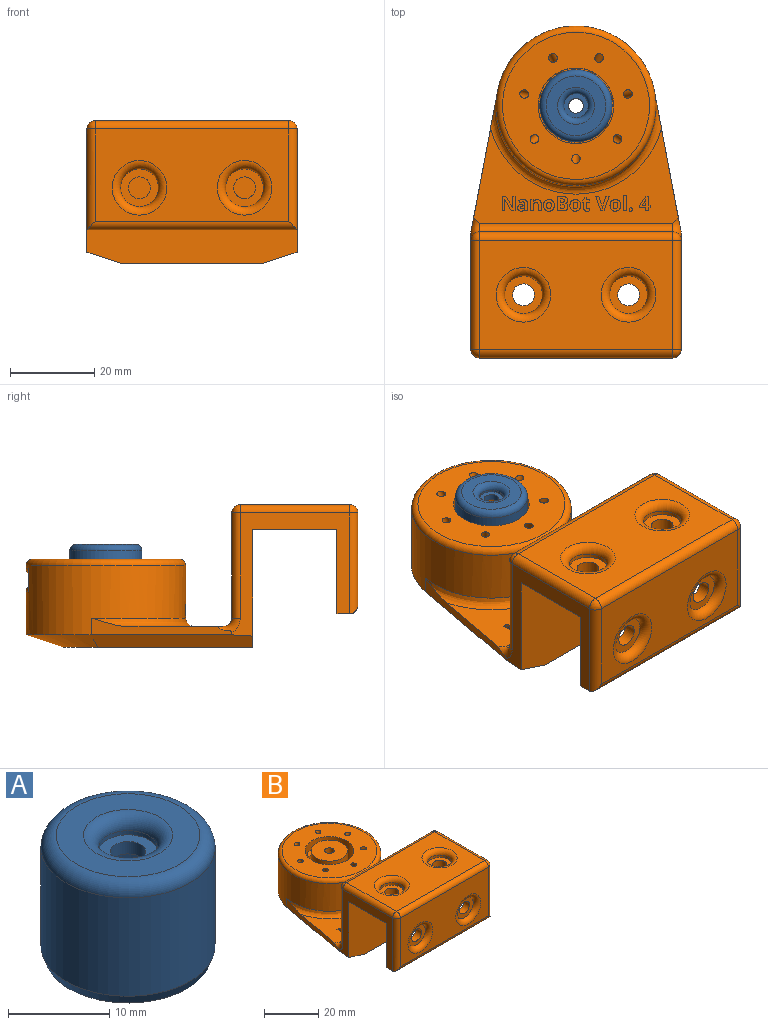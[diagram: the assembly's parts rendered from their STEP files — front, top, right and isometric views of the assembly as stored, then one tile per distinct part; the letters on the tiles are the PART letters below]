
ASSEMBLY  parts=2 mates=1
PART A: 12 faces, bbox 18.6x18.6x14.5 mm
  f0: cylinder r=1.75mm len=3.5mm, axis (0,0,-1), area 16.5mm2, adj f1,f7
  f1: plane 14.3x14.3mm, normal (0,0,-1), area 151mm2, adj f0,f4
  f2: cylinder r=8.6mm len=17.2mm, axis (0,0,-1), area 643.1mm2, adj f9,f11
  f3: plane 14.2x14.2mm, normal (0,0,1), area 97.5mm2, adj f10,f11
  f4: cylinder r=7.15mm len=14.3mm, axis (0,0,1), area 444.8mm2, adj f1,f8
  f5: plane 16.4x16.4mm, normal (0,0,-1), area 32.2mm2, adj f8,f9
  f6: cylinder r=2.9mm len=5.8mm, axis (0,0,1), area 9.1mm2, adj f7,f10
  f7: plane 5.8x5.8mm, normal (0,0,1), area 16.8mm2, adj f0,f6
  f8: cone r=7.55mm half-angle=20deg, axis (0,0,-1), area 54mm2, adj f4,f5
  f9: cone r=8.6mm half-angle=20deg, axis (0,0,1), area 61.7mm2, adj f2,f5
  f10: torus R=4.4mm, axis (0,0,1), area 51mm2, adj f3,f6
  f11: torus R=7.1mm, axis (0,0,1), area 119.2mm2, adj f2,f3
PART B: 294 faces, bbox 50.4x81x35.1 mm
  f0: plane 5.6x5.13mm, normal (0,0,1), area 23.1mm2, adj f2,f3,f282,f283,f288
  f1: plane 13.5x13.5mm, normal (0,0,1), area 133.5mm2, adj f275,f288
  f2: plane 10.14x5mm, normal (1,0,0), area 33.4mm2, adj f0,f4,f278,f280,f281,f283,f284,f288
  f3: plane 10.14x5mm, normal (-1,0,0), area 33.4mm2, adj f0,f4,f278,f280,f281,f282,f285,f288
  f4: plane 10.75x5.6mm, normal (0,0,-1), area 49.5mm2, adj f2,f3,f275,f280,f288
  f5: plane 8.95x5.66mm, normal (0,0,1), area 48mm2, adj f276,f277,f287,f289,f291,f292
  f6: cylinder r=1.75mm len=12.25mm, axis (0,0,1), area 134.7mm2, adj f33,f281
  f7: cylinder r=1mm len=22.37mm, axis (-0.27,-0.21,0.94), area 130.9mm2, adj f33,f35,f286,f287
  f8: cylinder r=1mm len=22.37mm, axis (-0.33,0.08,0.94), area 130.9mm2, adj f33,f35,f286,f287
  f9: cylinder r=1mm len=22.37mm, axis (-0.15,0.31,0.94), area 130.9mm2, adj f33,f35,f286,f287
  f10: cylinder r=1mm len=22.37mm, axis (0.15,0.31,0.94), area 130.9mm2, adj f33,f35,f286,f287
  f11: cylinder r=1mm len=22.37mm, axis (0.33,0.08,0.94), area 130.9mm2, adj f33,f35,f286,f287
  f12: cylinder r=1mm len=22.37mm, axis (0.27,-0.21,0.94), area 130.9mm2, adj f33,f35,f286,f287
  f13: plane 48.78x22.84mm, normal (0,0,1), area 488.2mm2, adj f36,f37,f38,f39,f44,f57,f62,f63
  f14: plane 29.31x28mm, normal (1,0,0), area 242.9mm2, adj f17,f21,f29,f32,f37,f40,f43,f44
  f15: plane 29.31x28mm, normal (-1,0,0), area 242.9mm2, adj f17,f21,f29,f32,f36,f42,f50,f54
  f16: plane 46x25mm, normal (0,1,0), area 1150mm2, adj f39,f47,f53,f56
  f17: plane 50x20mm, normal (0,0,-1), area 957.5mm2, adj f14,f15,f21,f22,f23,f32
  f18: plane 46x22mm, normal (0,-1,0), area 746.5mm2, adj f43,f46,f49,f50,f58,f59
  f19: cylinder r=2.6mm len=5.2mm, axis (0,-1,0), area 49mm2, adj f21,f31
  f20: cylinder r=2.6mm len=5.2mm, axis (0,-1,0), area 49mm2, adj f21,f30
  f21: plane 50x20mm, normal (0,1,0), area 957.5mm2, adj f14,f15,f17,f19,f20,f29
  f22: cylinder r=2.6mm len=5.2mm, axis (0,0,1), area 49mm2, adj f17,f28
  f23: cylinder r=2.6mm len=5.2mm, axis (0,0,1), area 49mm2, adj f17,f26
  f24: plane 46x26mm, normal (0,0,1), area 930.5mm2, adj f48,f49,f53,f54,f60,f61
  f25: cylinder r=4.5mm len=9mm, axis (0,0,1), area 28.3mm2, adj f26,f60
  f26: plane 9x9mm, normal (0,0,1), area 42.4mm2, adj f23,f25
  f27: cylinder r=4.5mm len=9mm, axis (0,0,1), area 28.3mm2, adj f28,f61
  f28: plane 9x9mm, normal (0,0,1), area 42.4mm2, adj f22,f27
  f29: plane 50x3mm, normal (0,0,-1), area 150mm2, adj f14,f15,f21,f46
  f30: plane 9x9mm, normal (0,-1,0), area 42.4mm2, adj f20,f59
  f31: plane 9x9mm, normal (0,-1,0), area 42.4mm2, adj f19,f58
  f32: plane 50x28mm, normal (0,-1,0), area 1377.9mm2, adj f14,f15,f17,f33,f40,f42
  f33: plane 45x33.57mm, normal (0,0,-1), area 1067.9mm2, adj f6,f7,f8,f9,f10,f11,f12,f32
  f34: cylinder r=19mm len=38mm, axis (0,0,-1), area 1650.8mm2, adj f36,f37,f38,f41,f289,f290,f291,f292
  f35: plane 35x35mm, normal (0,0,1), area 684.2mm2, adj f7,f8,f9,f10,f11,f12,f274,f287
  f36: plane 33.93x6.74mm, normal (-0.98,0.19,0), area 72.3mm2, adj f13,f15,f34,f38,f42,f57
  f37: plane 33.93x6.74mm, normal (0.98,0.19,0), area 72.3mm2, adj f13,f14,f34,f38,f40,f44
  f38: torus R=21mm, axis (0,0,1), area 190.1mm2, adj f13,f34,f36,f37
  f39: cylinder r=2mm len=46mm, axis (1,0,0), area 144.5mm2, adj f13,f16,f44,f57
  f40: plane 38.53x15.17mm, normal (0.31,0.06,-0.95), area 361.4mm2, adj f14,f32,f33,f37,f41
  f41: cone r=10mm half-angle=71.6deg, axis (0,0,1), area 380.8mm2, adj f33,f34,f40,f42
  f42: plane 38.53x15.17mm, normal (-0.31,0.06,-0.95), area 361.4mm2, adj f15,f32,f33,f36,f41
  f43: cylinder r=2mm len=24mm, axis (0,0,-1), area 73.1mm2, adj f14,f18,f45,f46
  f44: torus R=4mm, axis (1,0,0), area 13.1mm2, adj f13,f14,f37,f39,f47
  f45: sphere r=2mm, area 6.3mm2, adj f43,f48,f49
  f46: cylinder r=2mm len=50mm, axis (1,0,0), area 152.5mm2, adj f18,f29,f43,f50
  f47: cylinder r=2mm len=25mm, axis (0,0,1), area 78.5mm2, adj f14,f16,f44,f51
  f48: cylinder r=2mm len=26mm, axis (0,1,0), area 81.7mm2, adj f14,f24,f45,f51
  f49: cylinder r=2mm len=46mm, axis (1,0,0), area 144.5mm2, adj f18,f24,f45,f52
  f50: cylinder r=2mm len=24mm, axis (0,0,1), area 73.1mm2, adj f15,f18,f46,f52
  f51: sphere r=2mm, area 6.3mm2, adj f47,f48,f53
  f52: sphere r=2mm, area 6.3mm2, adj f49,f50,f54
  f53: cylinder r=2mm len=46mm, axis (-1,0,0), area 144.5mm2, adj f16,f24,f51,f55
  f54: cylinder r=2mm len=26mm, axis (0,-1,0), area 81.7mm2, adj f15,f24,f52,f55
  f55: sphere r=2mm, area 6.3mm2, adj f53,f54,f56
  f56: cylinder r=2mm len=25mm, axis (0,0,-1), area 78.5mm2, adj f15,f16,f55,f57
  f57: torus R=4mm, axis (1,0,0), area 13.1mm2, adj f13,f15,f36,f39,f56
  f58: torus R=6.5mm, axis (0,1,0), area 103.2mm2, adj f18,f31
  f59: torus R=6.5mm, axis (0,1,0), area 103.2mm2, adj f18,f30
  f60: torus R=6.5mm, axis (0,0,1), area 103.2mm2, adj f24,f25
  f61: torus R=6.5mm, axis (0,0,1), area 103.2mm2, adj f24,f27
  f62: extruded ~1x0.3mm, area 0.3mm2, adj f13,f63,f69,f70
  f63: extruded ~1x0.31mm, area 0.3mm2, adj f13,f62,f64,f70
  f64: extruded ~1x0.3mm, area 0.3mm2, adj f13,f63,f65,f70
  f65: extruded ~1x0.3mm, area 0.3mm2, adj f13,f64,f66,f70
  f66: extruded ~1x0.3mm, area 0.3mm2, adj f13,f65,f67,f70
  f67: extruded ~1x0.3mm, area 0.3mm2, adj f13,f66,f68,f70
  f68: extruded ~1x0.31mm, area 0.3mm2, adj f13,f67,f69,f70
  f69: extruded ~1x0.3mm, area 0.3mm2, adj f13,f62,f68,f70
  f70: plane 0.83x0.81mm, normal (0,0,1), area 0.6mm2, adj f62,f63,f64,f65,f66,f67,f68,f69
  f71: plane 1x0.51mm, normal (0,1,0), area 0.5mm2, adj f13,f72,f95,f96
  f72: plane 1.77x1mm, normal (-1,0,0), area 1.8mm2, adj f13,f71,f73,f96
  f73: extruded ~1x0.71mm, area 0.8mm2, adj f13,f72,f74,f96
  f74: extruded ~1x0.82mm, area 0.9mm2, adj f13,f73,f75,f96
  f75: extruded ~1.02x1mm, area 1.1mm2, adj f13,f74,f76,f96
  f76: plane 1x0.49mm, normal (0.9,0.44,0), area 0.5mm2, adj f13,f75,f77,f96
  f77: extruded ~1x0.75mm, area 0.8mm2, adj f13,f76,f78,f96
  f78: extruded ~1x0.41mm, area 0.7mm2, adj f13,f77,f79,f96
  f79: plane 1x0.12mm, normal (1,0,0), area 0.1mm2, adj f13,f78,f80,f96
  f80: plane 1x0.46mm, normal (0.03,-1,0), area 0.5mm2, adj f13,f79,f81,f96
  f81: extruded ~1x0.89mm, area 0.9mm2, adj f13,f80,f82,f96
  f82: extruded ~1x0.62mm, area 0.7mm2, adj f13,f81,f83,f96
  f83: extruded ~1x0.62mm, area 0.7mm2, adj f13,f82,f84,f96
  f84: extruded ~1x0.6mm, area 0.7mm2, adj f13,f83,f85,f96
  f85: extruded ~1x0.5mm, area 0.5mm2, adj f13,f84,f86,f96
  f86: extruded ~1x0.38mm, area 0.5mm2, adj f13,f85,f87,f96
  f87: plane 1x0.02mm, normal (0,1,0), area 0mm2, adj f13,f86,f95,f96
  f88: plane 1x0.22mm, normal (1,0,0), area 0.2mm2, adj f89,f94,f96,f97
  f89: extruded ~1x0.38mm, area 0.4mm2, adj f88,f90,f96,f97
  f90: extruded ~1x0.4mm, area 0.4mm2, adj f89,f91,f96,f97
  f91: extruded ~1x0.35mm, area 0.5mm2, adj f90,f92,f96,f97
  f92: extruded ~1x0.32mm, area 0.4mm2, adj f91,f93,f96,f97
  f93: extruded ~1x0.47mm, area 0.5mm2, adj f92,f94,f96,f97
  f94: plane 1x0.28mm, normal (-0.04,1,0), area 0.3mm2, adj f88,f93,f96,f97
  f95: plane 1x0.36mm, normal (0.93,0.36,0), area 0.4mm2, adj f13,f71,f87,f96
  f96: plane 2.76x2.37mm, normal (0,0,1), area 4.3mm2, adj f71,f72,f73,f74,f75,f76,f77,f78
  f97: plane 0.9x0.75mm, normal (0,0,1), area 0.5mm2, adj f88,f89,f90,f91,f92,f93,f94
  f98: extruded ~1x0.59mm, area 0.6mm2, adj f99,f115,f116,f271
  f99: extruded ~1x0.42mm, area 0.5mm2, adj f98,f100,f116,f271
  f100: extruded ~1x0.42mm, area 0.5mm2, adj f99,f101,f116,f271
  f101: extruded ~1x0.59mm, area 0.6mm2, adj f100,f102,f116,f271
  f102: extruded ~1x0.6mm, area 0.6mm2, adj f101,f103,f116,f271
  f103: extruded ~1x0.42mm, area 0.5mm2, adj f102,f104,f116,f271
  f104: extruded ~1x0.42mm, area 0.5mm2, adj f103,f115,f116,f271
  f105: extruded ~1x0.73mm, area 0.8mm2, adj f13,f106,f114,f116
  f106: extruded ~1x0.48mm, area 0.7mm2, adj f13,f105,f107,f116
  f107: extruded ~1x0.67mm, area 0.7mm2, adj f13,f106,f108,f116
  f108: extruded ~1x0.95mm, area 1.1mm2, adj f13,f107,f109,f116
  f109: extruded ~1.01x1mm, area 1.1mm2, adj f13,f108,f110,f116
  f110: extruded ~1x0.73mm, area 0.8mm2, adj f13,f109,f111,f116
  f111: extruded ~1x0.48mm, area 0.7mm2, adj f13,f110,f112,f116
  f112: extruded ~1x0.67mm, area 0.7mm2, adj f13,f111,f113,f116
  f113: extruded ~1x0.95mm, area 1.1mm2, adj f13,f112,f114,f116
  f114: extruded ~1.01x1mm, area 1.1mm2, adj f13,f105,f113,f116
  f115: extruded ~1x0.6mm, area 0.6mm2, adj f98,f104,f116,f271
  f116: plane 2.75x2.57mm, normal (0,0,1), area 4.3mm2, adj f98,f99,f100,f101,f102,f103,f104,f105
  f117: extruded ~1x0.59mm, area 0.6mm2, adj f118,f134,f135,f272
  f118: extruded ~1x0.42mm, area 0.5mm2, adj f117,f119,f135,f272
  f119: extruded ~1x0.42mm, area 0.5mm2, adj f118,f120,f135,f272
  f120: extruded ~1x0.59mm, area 0.6mm2, adj f119,f121,f135,f272
  f121: extruded ~1x0.6mm, area 0.6mm2, adj f120,f122,f135,f272
  f122: extruded ~1x0.42mm, area 0.5mm2, adj f121,f123,f135,f272
  f123: extruded ~1x0.42mm, area 0.5mm2, adj f122,f134,f135,f272
  f124: extruded ~1x0.73mm, area 0.8mm2, adj f13,f125,f133,f135
  f125: extruded ~1x0.48mm, area 0.7mm2, adj f13,f124,f126,f135
  f126: extruded ~1x0.67mm, area 0.7mm2, adj f13,f125,f127,f135
  f127: extruded ~1x0.95mm, area 1.1mm2, adj f13,f126,f128,f135
  f128: extruded ~1.01x1mm, area 1.1mm2, adj f13,f127,f129,f135
  f129: extruded ~1x0.73mm, area 0.8mm2, adj f13,f128,f130,f135
  f130: extruded ~1x0.48mm, area 0.7mm2, adj f13,f129,f131,f135
  f131: extruded ~1x0.67mm, area 0.7mm2, adj f13,f130,f132,f135
  f132: extruded ~1x0.95mm, area 1.1mm2, adj f13,f131,f133,f135
  f133: extruded ~1.01x1mm, area 1.1mm2, adj f13,f124,f132,f135
  f134: extruded ~1x0.6mm, area 0.6mm2, adj f117,f123,f135,f272
  f135: plane 2.75x2.57mm, normal (0,0,1), area 4.3mm2, adj f117,f118,f119,f120,f121,f122,f123,f124
  f136: plane 3.69x1mm, normal (-1,0,0), area 3.7mm2, adj f13,f137,f139,f140
  f137: plane 1x0.72mm, normal (0,-1,0), area 0.7mm2, adj f13,f136,f138,f140
  f138: plane 3.69x1mm, normal (1,0,0), area 3.7mm2, adj f13,f137,f139,f140
  f139: plane 1x0.72mm, normal (0,1,0), area 0.7mm2, adj f13,f136,f138,f140
  f140: plane 3.69x0.72mm, normal (0,0,1), area 2.7mm2, adj f136,f137,f138,f139
  f141: plane 2.07x1mm, normal (0.95,-0.3,0), area 2.2mm2, adj f13,f142,f150,f151
  f142: extruded ~1x0.76mm, area 0.8mm2, adj f13,f141,f143,f151
  f143: extruded ~1x0.34mm, area 0.3mm2, adj f13,f142,f144,f151
  f144: extruded ~1x0.43mm, area 0.4mm2, adj f13,f143,f145,f151
  f145: plane 2.07x1mm, normal (-0.95,-0.3,0), area 2.2mm2, adj f13,f144,f146,f151
  f146: plane 1x0.74mm, normal (0,-1,0), area 0.7mm2, adj f13,f145,f147,f151
  f147: plane 3.47x1.18mm, normal (0.95,0.32,0), area 3.7mm2, adj f13,f146,f148,f151
  f148: plane 1x0.8mm, normal (0,1,0), area 0.8mm2, adj f13,f147,f149,f151
  f149: plane 3.47x1.18mm, normal (-0.95,0.32,0), area 3.7mm2, adj f13,f148,f150,f151
  f150: plane 1x0.74mm, normal (0,-1,0), area 0.7mm2, adj f13,f141,f149,f151
  f151: plane 3.47x3.16mm, normal (0,0,1), area 4.6mm2, adj f141,f142,f143,f144,f145,f146,f147,f148
  f152: extruded ~1x0.23mm, area 0.2mm2, adj f13,f153,f169,f170
  f153: extruded ~1x0.23mm, area 0.3mm2, adj f13,f152,f154,f170
  f154: plane 1.28x1mm, normal (-1,0,0), area 1.3mm2, adj f13,f153,f155,f170
  f155: plane 1x0.74mm, normal (0,1,0), area 0.7mm2, adj f13,f154,f156,f170
  f156: plane 1x0.54mm, normal (-1,0,0), area 0.5mm2, adj f13,f155,f157,f170
  f157: plane 1x0.74mm, normal (0,-1,0), area 0.7mm2, adj f13,f156,f158,f170
  f158: plane 1x0.57mm, normal (-1,0,0), area 0.6mm2, adj f13,f157,f159,f170
  f159: plane 1x0.46mm, normal (0,-1,0), area 0.5mm2, adj f13,f158,f160,f170
  f160: plane 1x0.56mm, normal (0.94,-0.35,0), area 0.6mm2, adj f13,f159,f161,f170
  f161: plane 1x0.4mm, normal (0.52,-0.85,0), area 0.5mm2, adj f13,f160,f162,f170
  f162: plane 1x0.31mm, normal (1,0,0), area 0.3mm2, adj f13,f161,f163,f170
  f163: plane 1x0.35mm, normal (0,1,0), area 0.3mm2, adj f13,f162,f164,f170
  f164: plane 1.28x1mm, normal (1,0,0), area 1.3mm2, adj f13,f163,f165,f170
  f165: extruded ~1x0.66mm, area 0.7mm2, adj f13,f164,f166,f170
  f166: extruded ~1x0.63mm, area 0.7mm2, adj f13,f165,f167,f170
  f167: extruded ~1x0.66mm, area 0.7mm2, adj f13,f166,f168,f170
  f168: plane 1x0.54mm, normal (-1,0,0), area 0.5mm2, adj f13,f167,f169,f170
  f169: extruded ~1x0.46mm, area 0.5mm2, adj f13,f152,f168,f170
  f170: plane 3.27x1.84mm, normal (0,0,1), area 3.2mm2, adj f152,f153,f154,f155,f156,f157,f158,f159
  f171: plane 1.73x1mm, normal (-1,0,0), area 1.7mm2, adj f13,f172,f187,f188
  f172: extruded ~1x0.72mm, area 0.8mm2, adj f13,f171,f173,f188
  f173: extruded ~1x0.7mm, area 0.8mm2, adj f13,f172,f174,f188
  f174: extruded ~1x0.48mm, area 0.5mm2, adj f13,f173,f175,f188
  f175: extruded ~1x0.33mm, area 0.4mm2, adj f13,f174,f176,f188
  f176: plane 1x0.04mm, normal (0,-1,0), area 0mm2, adj f13,f175,f177,f188
  f177: plane 1x0.34mm, normal (-0.96,-0.28,0), area 0.4mm2, adj f13,f176,f178,f188
  f178: plane 1x0.55mm, normal (0,-1,0), area 0.6mm2, adj f13,f177,f179,f188
  f179: plane 2.65x1mm, normal (1,0,0), area 2.7mm2, adj f13,f178,f180,f188
  f180: plane 1x0.72mm, normal (0,1,0), area 0.7mm2, adj f13,f179,f181,f188
  f181: plane 1.25x1mm, normal (-1,0,0), area 1.2mm2, adj f13,f180,f182,f188
  f182: extruded ~1x0.67mm, area 0.7mm2, adj f13,f181,f183,f188
  f183: extruded ~1x0.44mm, area 0.5mm2, adj f13,f182,f184,f188
  f184: extruded ~1x0.33mm, area 0.4mm2, adj f13,f183,f185,f188
  f185: extruded ~1x0.43mm, area 0.4mm2, adj f13,f184,f186,f188
  f186: plane 1.55x1mm, normal (1,0,0), area 1.6mm2, adj f13,f185,f187,f188
  f187: plane 1x0.72mm, normal (0,1,0), area 0.7mm2, adj f13,f171,f186,f188
  f188: plane 2.7x2.45mm, normal (0,0,1), area 4.3mm2, adj f171,f172,f173,f174,f175,f176,f177,f178
  f189: extruded ~1x0.59mm, area 0.6mm2, adj f190,f206,f207,f273
  f190: extruded ~1x0.42mm, area 0.5mm2, adj f189,f191,f207,f273
  f191: extruded ~1x0.42mm, area 0.5mm2, adj f190,f192,f207,f273
  f192: extruded ~1x0.59mm, area 0.6mm2, adj f191,f193,f207,f273
  f193: extruded ~1x0.6mm, area 0.6mm2, adj f192,f194,f207,f273
  f194: extruded ~1x0.42mm, area 0.5mm2, adj f193,f195,f207,f273
  f195: extruded ~1x0.42mm, area 0.5mm2, adj f194,f206,f207,f273
  f196: extruded ~1x0.73mm, area 0.8mm2, adj f13,f197,f205,f207
  f197: extruded ~1x0.48mm, area 0.7mm2, adj f13,f196,f198,f207
  f198: extruded ~1x0.67mm, area 0.7mm2, adj f13,f197,f199,f207
  f199: extruded ~1x0.95mm, area 1.1mm2, adj f13,f198,f200,f207
  f200: extruded ~1.01x1mm, area 1.1mm2, adj f13,f199,f201,f207
  f201: extruded ~1x0.73mm, area 0.8mm2, adj f13,f200,f202,f207
  f202: extruded ~1x0.48mm, area 0.7mm2, adj f13,f201,f203,f207
  f203: extruded ~1x0.67mm, area 0.7mm2, adj f13,f202,f204,f207
  f204: extruded ~1x0.95mm, area 1.1mm2, adj f13,f203,f205,f207
  f205: extruded ~1.01x1mm, area 1.1mm2, adj f13,f196,f204,f207
  f206: extruded ~1x0.6mm, area 0.6mm2, adj f189,f195,f207,f273
  f207: plane 2.75x2.57mm, normal (0,0,1), area 4.3mm2, adj f189,f190,f191,f192,f193,f194,f195,f196
  f208: plane 1x0.57mm, normal (-1,0,0), area 0.6mm2, adj f13,f209,f225,f226
  f209: plane 1x0.42mm, normal (0,-1,0), area 0.4mm2, adj f13,f208,f210,f226
  f210: plane 2.18x1mm, normal (-1,0,0), area 2.2mm2, adj f13,f209,f211,f226
  f211: plane 1x0.68mm, normal (0,-1,0), area 0.7mm2, adj f13,f210,f212,f226
  f212: plane 2.24x1.52mm, normal (0.83,-0.56,0), area 2.7mm2, adj f13,f211,f213,f226
  f213: plane 1x0.51mm, normal (1,0,0), area 0.5mm2, adj f13,f212,f214,f226
  f214: plane 1.48x1mm, normal (0,1,0), area 1.5mm2, adj f13,f213,f215,f226
  f215: plane 1x0.72mm, normal (1,0,0), area 0.7mm2, adj f13,f214,f216,f226
  f216: plane 1x0.72mm, normal (0,1,0), area 0.7mm2, adj f13,f215,f217,f226
  f217: plane 1x0.72mm, normal (-1,0,0), area 0.7mm2, adj f13,f216,f225,f226
  f218: plane 1x0.84mm, normal (0,-1,0), area 0.8mm2, adj f219,f224,f226,f227
  f219: plane 1x0.96mm, normal (-0.83,0.55,0), area 1.2mm2, adj f218,f220,f226,f227
  f220: extruded ~1x0.38mm, area 0.4mm2, adj f219,f221,f226,f227
  f221: plane 1x0.02mm, normal (0,1,0), area 0mm2, adj f220,f222,f226,f227
  f222: extruded ~1x0.33mm, area 0.3mm2, adj f221,f223,f226,f227
  f223: extruded ~1x0.43mm, area 0.4mm2, adj f222,f224,f226,f227
  f224: plane 1x0.59mm, normal (1,0,0), area 0.6mm2, adj f218,f223,f226,f227
  f225: plane 1x0.42mm, normal (0,1,0), area 0.4mm2, adj f13,f208,f217,f226
  f226: plane 3.47x2.62mm, normal (0,0,1), area 4.6mm2, adj f208,f209,f210,f211,f212,f213,f214,f215
  f227: plane 1.34x0.87mm, normal (0,0,1), area 0.5mm2, adj f218,f219,f220,f221,f222,f223,f224
  f228: plane 3.47x1mm, normal (1,0,0), area 3.5mm2, adj f13,f229,f252,f253
  f229: plane 1.3x1mm, normal (0,1,0), area 1.3mm2, adj f13,f228,f230,f253
  f230: extruded ~1x0.93mm, area 1mm2, adj f13,f229,f231,f253
  f231: extruded ~1x0.74mm, area 0.8mm2, adj f13,f230,f232,f253
  f232: extruded ~1x0.54mm, area 0.6mm2, adj f13,f231,f233,f253
  f233: extruded ~1x0.48mm, area 0.6mm2, adj f13,f232,f234,f253
  f234: plane 1x0.02mm, normal (-1,0,0), area 0mm2, adj f13,f233,f235,f253
  f235: extruded ~1x0.39mm, area 0.5mm2, adj f13,f234,f236,f253
  f236: extruded ~1x0.51mm, area 0.5mm2, adj f13,f235,f237,f253
  f237: extruded ~1x0.67mm, area 0.8mm2, adj f13,f236,f238,f253
  f238: extruded ~1.07x1mm, area 1.1mm2, adj f13,f237,f252,f253
  f239: plane 1x0.77mm, normal (-1,0,0), area 0.8mm2, adj f240,f250,f253,f255
  f240: plane 1x0.39mm, normal (0,1,0), area 0.4mm2, adj f239,f241,f253,f255
  f241: extruded ~1x0.46mm, area 0.5mm2, adj f240,f242,f253,f255
  f242: extruded ~1x0.29mm, area 0.3mm2, adj f241,f243,f253,f255
  f243: extruded ~1x0.31mm, area 0.3mm2, adj f242,f244,f253,f255
  f244: extruded ~1x0.43mm, area 0.4mm2, adj f243,f250,f253,f255
  f245: plane 1x0.46mm, normal (0,1,0), area 0.5mm2, adj f246,f251,f253,f254
  f246: extruded ~1x0.62mm, area 0.9mm2, adj f245,f247,f253,f254
  f247: extruded ~1x0.36mm, area 0.4mm2, adj f246,f248,f253,f254
  f248: extruded ~1x0.45mm, area 0.5mm2, adj f247,f249,f253,f254
  f249: plane 1x0.48mm, normal (0,-1,0), area 0.5mm2, adj f248,f251,f253,f254
  f250: plane 1x0.43mm, normal (0,-1,0), area 0.4mm2, adj f239,f244,f253,f255
  f251: plane 1x0.9mm, normal (-1,0,0), area 0.9mm2, adj f245,f249,f253,f254
  f252: plane 1.08x1mm, normal (0,-1,0), area 1.1mm2, adj f13,f228,f238,f253
  f253: plane 3.47x2.57mm, normal (0,0,1), area 6.6mm2, adj f228,f229,f230,f231,f232,f233,f234,f235
  f254: plane 1.07x0.9mm, normal (0,0,1), area 0.9mm2, adj f245,f246,f247,f248,f249,f251
  f255: plane 0.99x0.77mm, normal (0,0,1), area 0.7mm2, adj f239,f240,f241,f242,f243,f244,f250
  f256: plane 3.47x1mm, normal (-1,0,0), area 3.5mm2, adj f13,f257,f269,f270
  f257: plane 1x0.66mm, normal (0,-1,0), area 0.7mm2, adj f13,f256,f258,f270
  f258: plane 1.64x1mm, normal (1,0,0), area 1.6mm2, adj f13,f257,f259,f270
  f259: extruded ~1x0.96mm, area 1mm2, adj f13,f258,f260,f270
  f260: plane 1x0.02mm, normal (0,-1,0), area 0mm2, adj f13,f259,f261,f270
  f261: plane 2.6x1.51mm, normal (-0.87,-0.5,0), area 3mm2, adj f13,f260,f262,f270
  f262: plane 1x0.93mm, normal (0,-1,0), area 0.9mm2, adj f13,f261,f263,f270
  f263: plane 3.47x1mm, normal (1,0,0), area 3.5mm2, adj f13,f262,f264,f270
  f264: plane 1x0.66mm, normal (0,1,0), area 0.7mm2, adj f13,f263,f265,f270
  f265: plane 1.63x1mm, normal (-1,0,0), area 1.6mm2, adj f13,f264,f266,f270
  f266: extruded ~1x0.99mm, area 1mm2, adj f13,f265,f267,f270
  f267: plane 1x0.02mm, normal (0,1,0), area 0mm2, adj f13,f266,f268,f270
  f268: plane 2.63x1.51mm, normal (0.87,0.5,0), area 3mm2, adj f13,f267,f269,f270
  f269: plane 1x0.94mm, normal (0,1,0), area 0.9mm2, adj f13,f256,f268,f270
  f270: plane 3.47x3.08mm, normal (0,0,1), area 6.8mm2, adj f256,f257,f258,f259,f260,f261,f262,f263
  f271: plane 1.59x1.09mm, normal (0,0,1), area 1.5mm2, adj f98,f99,f100,f101,f102,f103,f104,f115
  f272: plane 1.59x1.09mm, normal (0,0,1), area 1.5mm2, adj f117,f118,f119,f120,f121,f122,f123,f134
  f273: plane 1.59x1.09mm, normal (0,0,1), area 1.5mm2, adj f189,f190,f191,f192,f193,f194,f195,f206
  f274: cylinder r=1mm len=22.37mm, axis (0,-0.34,0.94), area 130.9mm2, adj f33,f35,f286,f287
  f275: cylinder r=1.75mm len=3.75mm, axis (0,0,1), area 41.2mm2, adj f1,f4
  f276: plane 8.41x2.5mm, normal (1,0,0), area 21mm2, adj f5,f279,f287,f292
  f277: plane 8.41x2.5mm, normal (-1,0,0), area 21mm2, adj f5,f279,f287,f289
  f278: plane 5.6x2.38mm, normal (0,0,1), area 8.8mm2, adj f2,f3,f280,f284,f285
  f279: plane 8.95x5.66mm, normal (0,0,-1), area 48mm2, adj f276,f277,f287,f289,f290,f292
  f280: plane 5.6x2.5mm, normal (0,1,0), area 14mm2, adj f2,f3,f4,f278
  f281: plane 6.47x5.6mm, normal (0,0,1), area 17.5mm2, adj f2,f3,f6,f282,f283,f284,f285
  f282: plane 2.8x2.5mm, normal (-0.5,-0.87,0), area 8.1mm2, adj f0,f3,f281,f283
  f283: plane 2.8x2.5mm, normal (0.5,-0.87,0), area 8.1mm2, adj f0,f2,f281,f282
  f284: plane 2.8x2.5mm, normal (0.5,0.87,0), area 8.1mm2, adj f2,f278,f281,f285
  f285: plane 2.8x2.5mm, normal (-0.5,0.87,0), area 8.1mm2, adj f3,f278,f281,f284
  f286: plane 18x17.95mm, normal (0,0,1), area 94.9mm2, adj f7,f8,f9,f10,f11,f12,f274,f287
  f287: cylinder r=9mm len=18mm, axis (0,0,1), area 562.2mm2, adj f5,f7,f8,f9,f10,f11,f12,f35
  f288: cylinder r=6.75mm len=13.5mm, axis (0,0,1), area 452.1mm2, adj f0,f1,f2,f3,f4,f286
  f289: cylinder r=1.5mm len=5.5mm, axis (0,0,-1), area 9.5mm2, adj f5,f34,f277,f279,f290,f291
  f290: torus R=17.5mm, axis (0,0,1), area 17mm2, adj f34,f279,f289,f292
  f291: torus R=17.5mm, axis (0,0,1), area 17mm2, adj f5,f34,f289,f292
  f292: cylinder r=1.5mm len=5.5mm, axis (0,0,-1), area 9.5mm2, adj f5,f34,f276,f279,f290,f291
  f293: torus R=17.5mm, axis (0,0,1), area 273.2mm2, adj f34,f35
PLACE A t=(61.5,-23.31,23.37)mm
PLACE B t=(11.5,-23.31,23.37)mm
MATE fastened A.f0 <-> B.f287  axis (0,0,1) through (11.5,21.69,13.87)mm
